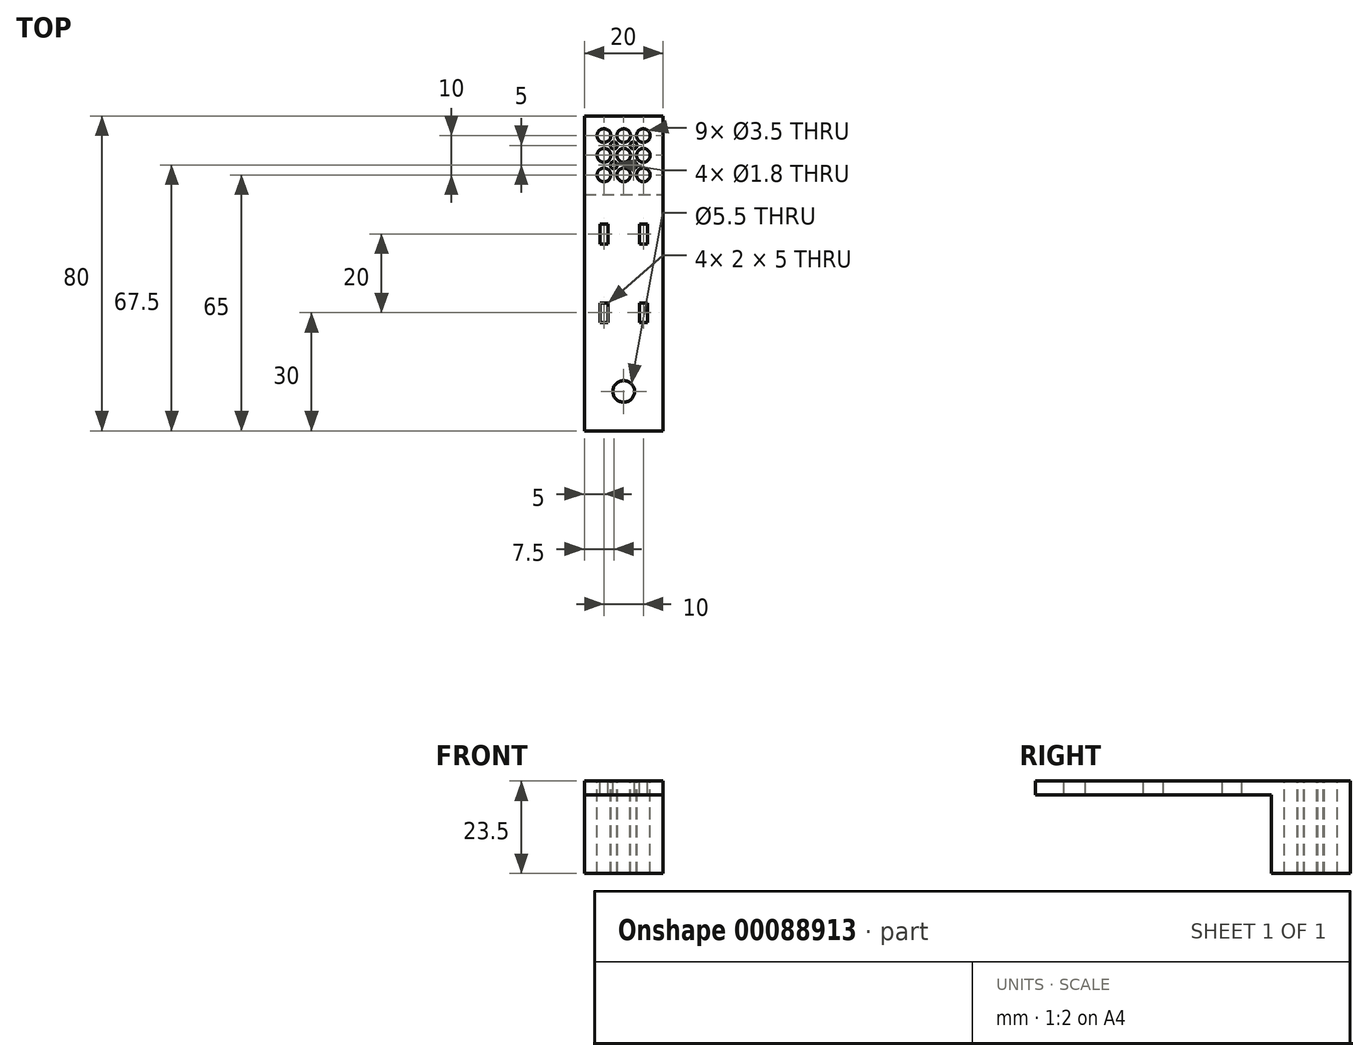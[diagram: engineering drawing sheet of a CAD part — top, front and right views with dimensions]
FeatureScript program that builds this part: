
annotation { "Feature Type Name" : "Feature", "Feature Type Description" : "" }
export const myFeature = defineFeature(function(context is Context, id is Id, definition is map)
    precondition{}
    {
        {
            var Q0;
            Q0=qCreatedBy(makeId("Top.planeOp"),FACE);
            var sketch = newSketch(context, id + "F0", { "sketchPlane" : qUnion([Q0])});
            skLineSegment(sketch, "E0.bottom", {"start": v(0, 0) * mm, "end": v(20, 0) * mm});
            skLineSegment(sketch, "E0.top", {"start": v(0, 20) * mm, "end": v(20, 20) * mm});
            skLineSegment(sketch, "E0.left", {"start": v(0, 0) * mm, "end": v(0, 20) * mm});
            skLineSegment(sketch, "E0.right", {"start": v(20, 0) * mm, "end": v(20, 20) * mm});
            skSolve(sketch);
        }
        {
            var Q0;
            Q0=qSketchRegion(id+"F0",true);
            extrude(context, id + "F1", {"entities" : qUnion([Q0]), "depth" : 20 * mm});
        }
        {
            var Q0;
            Q0=makeQuery(id+"F1.opExtrude","SWEPT_FACE",FACE,{"disambiguationData":[OSD([sQuery(id+"F0.wireOp",EDGE,"E0.top")])]});
            var sketch = newSketch(context, id + "F2", { "sketchPlane" : qUnion([Q0])});
            skLineSegment(sketch, "E1.bottom", {"start": v(-20, 20) * mm, "end": v(0, 20) * mm});
            skLineSegment(sketch, "E1.top", {"start": v(-20, 23.5) * mm, "end": v(0, 23.5) * mm});
            skLineSegment(sketch, "E1.left", {"start": v(-20, 20) * mm, "end": v(-20, 23.5) * mm});
            skLineSegment(sketch, "E1.right", {"start": v(0, 20) * mm, "end": v(0, 23.5) * mm});
            skSolve(sketch);
        }
        {
            var Q0;
            Q0=qSketchRegion(id+"F2",true);
            extrude(context, id + "F3", {"entities" : qUnion([Q0]), "operationType" : NewBodyOperationType.ADD, "oppositeDirection" : true, "depth" : 80 * mm});
        }
        {
            var Q0;
            Q0=makeQuery(id+"F3.opExtrude","SWEPT_FACE",FACE,{"disambiguationData":[OSD([sQuery(id+"F2.wireOp",EDGE,"E1.top")])]});
            var sketch = newSketch(context, id + "F4", { "sketchPlane" : qUnion([Q0])});
            skLineSegment(sketch, "E2", {"start": v(0, -40) * mm, "end": v(20, -60) * mm, "construction": true});
            skLineSegment(sketch, "E3", {"start": v(0, -60) * mm, "end": v(20, -40) * mm, "construction": true});
            skCircle(sketch, "E4", {"center": v(10, -50) * mm, "radius": 2.75 * mm});
            skLineSegment(sketch, "E5", {"start": v(-26.09, -40) * mm, "end": v(57, -40) * mm, "construction": true});
            skLineSegment(sketch, "E6", {"start": v(10, 31.63) * mm, "end": v(10, -78.16) * mm, "construction": true});
            skLineSegment(sketch, "E7.bottom", {"start": v(4, -7.5) * mm, "end": v(6, -7.5) * mm});
            skLineSegment(sketch, "E7.top", {"start": v(4, -12.5) * mm, "end": v(6, -12.5) * mm});
            skLineSegment(sketch, "E7.left", {"start": v(4, -7.5) * mm, "end": v(4, -12.5) * mm});
            skLineSegment(sketch, "E7.right", {"start": v(6, -7.5) * mm, "end": v(6, -12.5) * mm});
            skLineSegment(sketch, "E8", {"start": v(5, 30.35) * mm, "end": v(5, -68.2) * mm, "construction": true});
            skLineSegment(sketch, "E9", {"start": v(-25.14, -20) * mm, "end": v(44.55, -20) * mm, "construction": true});
            skLineSegment(sketch, "E10.MirrorCS", {"start": v(4, -27.5) * mm, "end": v(6, -27.5) * mm});
            skLineSegment(sketch, "E11.MirrorCS", {"start": v(4, -32.5) * mm, "end": v(6, -32.5) * mm});
            skLineSegment(sketch, "E12.MirrorCS", {"start": v(4, -32.5) * mm, "end": v(4, -27.5) * mm});
            skLineSegment(sketch, "E13.MirrorCS", {"start": v(6, -32.5) * mm, "end": v(6, -27.5) * mm});
            skLineSegment(sketch, "E14.MirrorCS", {"start": v(16, -12.5) * mm, "end": v(14, -12.5) * mm});
            skLineSegment(sketch, "E15.MirrorCS", {"start": v(16, -27.5) * mm, "end": v(14, -27.5) * mm});
            skLineSegment(sketch, "E16.MirrorCS", {"start": v(16, -7.5) * mm, "end": v(14, -7.5) * mm});
            skLineSegment(sketch, "E17.MirrorCS", {"start": v(16, -32.5) * mm, "end": v(14, -32.5) * mm});
            skLineSegment(sketch, "E18.MirrorCS", {"start": v(14, -7.5) * mm, "end": v(14, -12.5) * mm});
            skLineSegment(sketch, "E19.MirrorCS", {"start": v(16, -32.5) * mm, "end": v(16, -27.5) * mm});
            skLineSegment(sketch, "E20.MirrorCS", {"start": v(16, -7.5) * mm, "end": v(16, -12.5) * mm});
            skLineSegment(sketch, "E21.MirrorCS", {"start": v(14, -32.5) * mm, "end": v(14, -27.5) * mm});
            skLineSegment(sketch, "E22", {"start": v(-26.56, -30) * mm, "end": v(48.46, -30) * mm, "construction": true});
            skSolve(sketch);
        }
        {
            var Q0;
            Q0=qSketchRegion(id+"F4",true);
            extrude(context, id + "F5", {"entities" : qUnion([Q0]), "operationType" : NewBodyOperationType.REMOVE, "endBound" : BoundingType.UP_TO_NEXT, "oppositeDirection" : true, "depth" : 25 * mm});
        }
        {
            var Q0;
            Q0=makeQuery(id+"F3.opExtrude","SWEPT_FACE",FACE,{"disambiguationData":[OSD([sQuery(id+"F2.wireOp",EDGE,"E1.top")])]});
            var sketch = newSketch(context, id + "F6", { "sketchPlane" : qUnion([Q0])});
            skCircle(sketch, "E23", {"center": v(5, 15) * mm, "radius": 1.75 * mm});
            skCircle(sketch, "E24.1.0.0", {"center": v(10, 15) * mm, "radius": 1.75 * mm});
            skCircle(sketch, "E24.2.0.0", {"center": v(15, 15) * mm, "radius": 1.75 * mm});
            skLineSegment(sketch, "E24.direction1", {"start": v(5, 15) * mm, "end": v(10, 15) * mm, "construction": true});
            skCircle(sketch, "E25.1.0.0", {"center": v(5, 10) * mm, "radius": 1.75 * mm});
            skCircle(sketch, "E25.1.0.1", {"center": v(10, 10) * mm, "radius": 1.75 * mm});
            skCircle(sketch, "E25.1.0.2", {"center": v(15, 10) * mm, "radius": 1.75 * mm});
            skLineSegment(sketch, "E25.1.0.3", {"start": v(5, 10) * mm, "end": v(10, 10) * mm, "construction": true});
            skCircle(sketch, "E25.2.0.0", {"center": v(5, 5) * mm, "radius": 1.75 * mm});
            skCircle(sketch, "E25.2.0.1", {"center": v(10, 5) * mm, "radius": 1.75 * mm});
            skCircle(sketch, "E25.2.0.2", {"center": v(15, 5) * mm, "radius": 1.75 * mm});
            skLineSegment(sketch, "E25.2.0.3", {"start": v(5, 5) * mm, "end": v(10, 5) * mm, "construction": true});
            skLineSegment(sketch, "E25.direction1", {"start": v(5, 15) * mm, "end": v(5, 10) * mm, "construction": true});
            skLineSegment(sketch, "E26", {"start": v(10, 28.07) * mm, "end": v(10, -24.7) * mm, "construction": true});
            skLineSegment(sketch, "E27", {"start": v(0, 0) * mm, "end": v(20, 20) * mm, "construction": true});
            skCircle(sketch, "E28", {"center": v(7.5, 12.5) * mm, "radius": 0.9 * mm});
            skCircle(sketch, "E29.0.1.0", {"center": v(7.5, 7.5) * mm, "radius": 0.9 * mm});
            skCircle(sketch, "E29.1.0.0", {"center": v(12.5, 12.5) * mm, "radius": 0.9 * mm});
            skCircle(sketch, "E29.1.1.0", {"center": v(12.5, 7.5) * mm, "radius": 0.9 * mm});
            skLineSegment(sketch, "E29.direction1", {"start": v(7.5, 12.5) * mm, "end": v(12.5, 12.5) * mm, "construction": true});
            skLineSegment(sketch, "E29.direction2", {"start": v(7.5, 12.5) * mm, "end": v(7.5, 7.5) * mm, "construction": true});
            skLineSegment(sketch, "E30", {"start": v(5, 15) * mm, "end": v(10, 10) * mm, "construction": true});
            skLineSegment(sketch, "E31", {"start": v(5, 10) * mm, "end": v(10, 15) * mm, "construction": true});
            skSolve(sketch);
        }
        {
            var Q0;
            Q0=qSketchRegion(id+"F6",true);
            extrude(context, id + "F7", {"entities" : qUnion([Q0]), "operationType" : NewBodyOperationType.REMOVE, "endBound" : BoundingType.UP_TO_NEXT, "oppositeDirection" : true, "depth" : 25 * mm});
        }
    });
